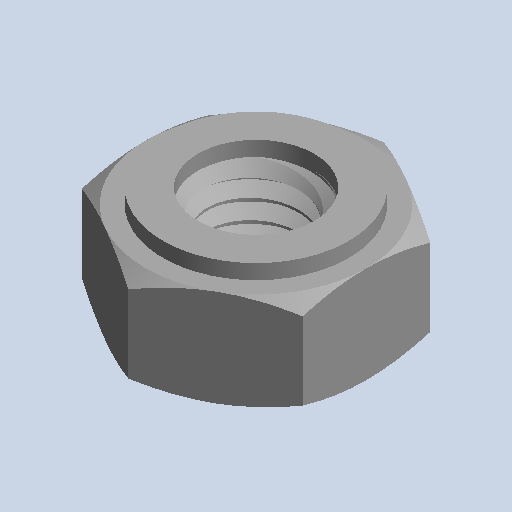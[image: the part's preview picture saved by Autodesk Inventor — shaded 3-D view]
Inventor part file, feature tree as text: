
AUTODESK INVENTOR PART (.ipt)
format: ipt  version: 2022.1 (Build 261234000, 234)  size: 218,624 bytes
history: native  units: mm (DEFAULTED — no unit token found)
features: other x8, mirror x1
bodies: Body1 (feature_tree)
feature tree (9):
  other  "Sólido1"
  other  "Origen"
  other  "Plano YZ"
  other  "Plano XZ"
  other  "Plano XY"
  other  "Eje X"
  other  "Eje Y"
  other  "Eje Z"
  mirror  "Mirror1"
